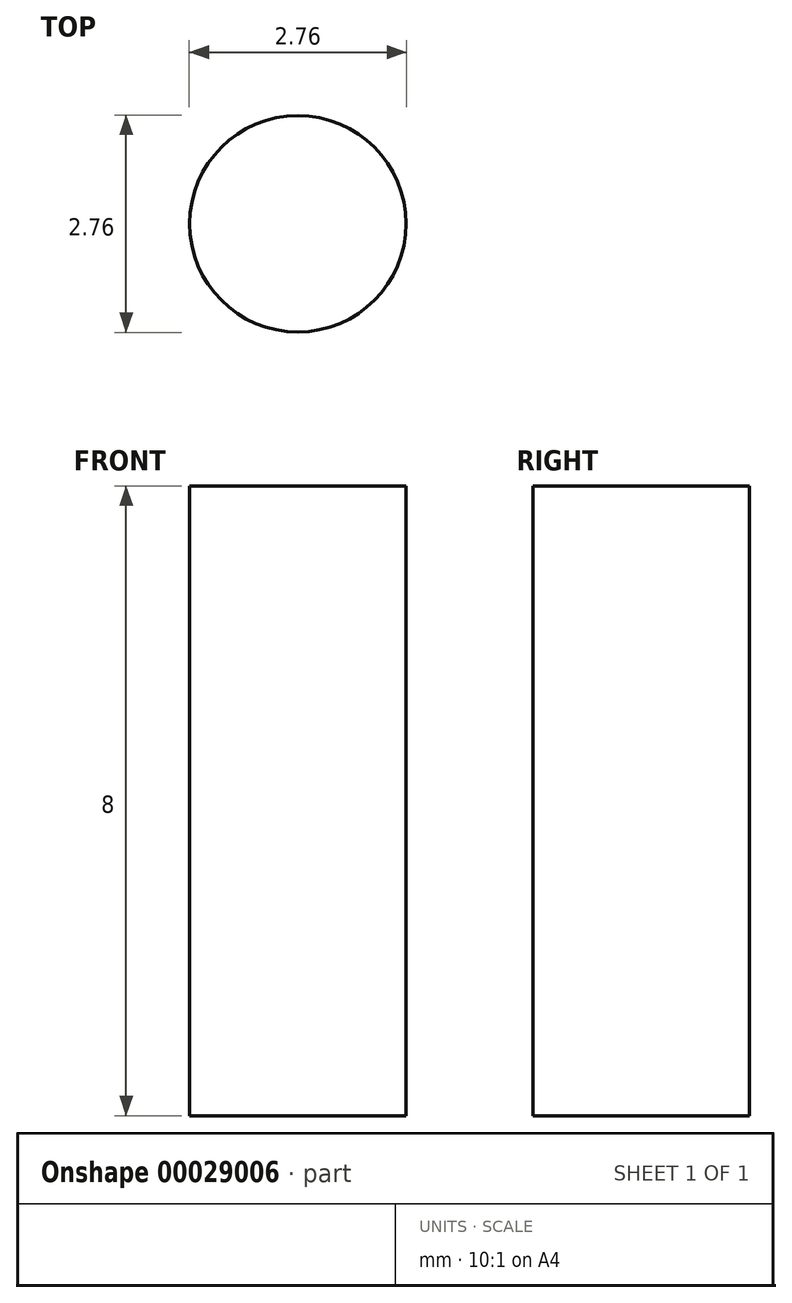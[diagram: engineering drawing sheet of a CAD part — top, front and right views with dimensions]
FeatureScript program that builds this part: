
annotation { "Feature Type Name" : "Feature", "Feature Type Description" : "" }
export const myFeature = defineFeature(function(context is Context, id is Id, definition is map)
    precondition{}
    {
        {
            var Q0;
            Q0=qCreatedBy(makeId("Top.planeOp"),FACE);
            var sketch = newSketch(context, id + "F0", { "sketchPlane" : qUnion([Q0])});
            skCircle(sketch, "E0", {"center": v(0, 0) * mm, "radius": 1.38 * mm});
            skSolve(sketch);
        }
        {
            var Q0;
            Q0 = qSketchRegion(id + "F0", true);
            extrude(context, id + "F1", {"entities" : qUnion([Q0]), "depth" : 8 * mm});
        }
    });
